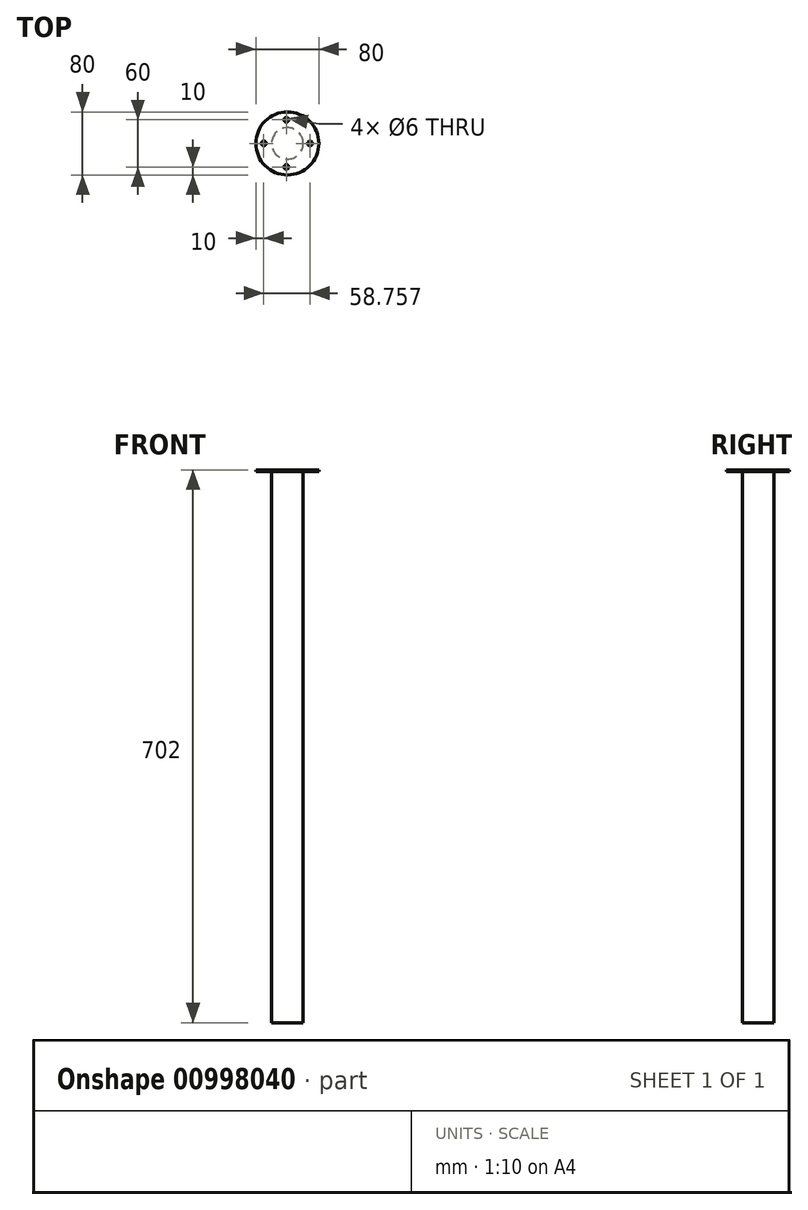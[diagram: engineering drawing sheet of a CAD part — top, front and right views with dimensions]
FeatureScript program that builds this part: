
annotation { "Feature Type Name" : "Feature", "Feature Type Description" : "" }
export const myFeature = defineFeature(function(context is Context, id is Id, definition is map)
    precondition{}
    {
        {
            var Q0;
            Q0=qCreatedBy(makeId("Top.planeOp"),FACE);
            var sketch = newSketch(context, id + "F0", { "sketchPlane" : qUnion([Q0])});
            skCircle(sketch, "E0", {"center": v(0, 0) * mm, "radius": 20 * mm});
            skSolve(sketch);
        }
        {
            var Q0;
            Q0=makeQuery(id+"F0.imprint","IMPRINT",FACE,{"disambiguationData":[TD([[makeQuery(id+"F0.imprint","IMPRINT",EDGE,{"derivedFrom":sQuery(id+"F0.wireOp",EDGE,"E0")}),1.0]])]});
            var Q1;
            Q1=sQuery(id+"F0.wireOp",EDGE,"E0");
            extrude(context, id + "F1", {"entities" : qUnion([Q0]), "surfaceEntities" : qUnion([Q1]), "oppositeDirection" : true, "depth" : 700 * mm, "offsetDistance" : 25 * mm});
        }
        {
            var Q0;
            Q0=qCreatedBy(makeId("Top.planeOp"),FACE);
            var sketch = newSketch(context, id + "F2", { "sketchPlane" : qUnion([Q0])});
            skCircle(sketch, "E1", {"center": v(0, 0) * mm, "radius": 40 * mm});
            skCircle(sketch, "E2", {"center": v(-30, 0) * mm, "radius": 3 * mm});
            skCircle(sketch, "E3.1.0", {"center": v(-1.24, -30) * mm, "radius": 3 * mm});
            skCircle(sketch, "E3.2.0", {"center": v(28.76, 0) * mm, "radius": 3 * mm});
            skCircle(sketch, "E3.3.0", {"center": v(-1.24, 30) * mm, "radius": 3 * mm});
            skSolve(sketch);
        }
        {
            var Q0;
            Q0 = qSketchRegion(id + "F2", true);
            extrude(context, id + "F3", {"entities" : qUnion([Q0]), "depth" : 2 * mm, "offsetDistance" : 25 * mm});
        }
    });
